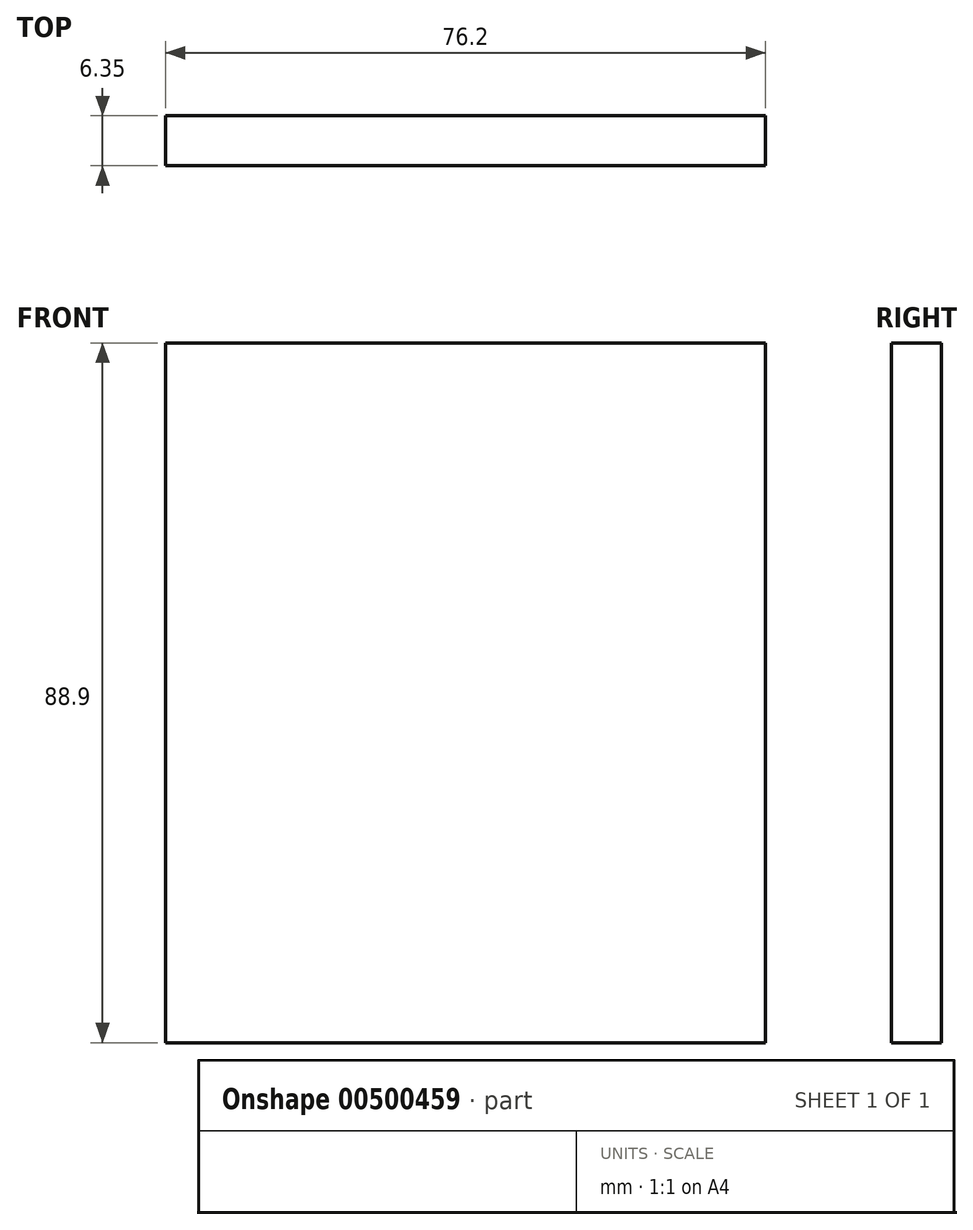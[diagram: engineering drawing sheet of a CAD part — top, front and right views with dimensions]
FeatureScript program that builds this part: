
annotation { "Feature Type Name" : "Feature", "Feature Type Description" : "" }
export const myFeature = defineFeature(function(context is Context, id is Id, definition is map)
    precondition{}
    {
        {
            var Q0;
            Q0=qCreatedBy(makeId("Front.planeOp"),FACE);
            var sketch = newSketch(context, id + "F0", { "sketchPlane" : qUnion([Q0])});
            skLineSegment(sketch, "E0.bottom", {"start": v(-36.9, 58.36) * mm, "end": v(39.3, 58.36) * mm});
            skLineSegment(sketch, "E0.top", {"start": v(-36.9, -30.54) * mm, "end": v(39.3, -30.54) * mm});
            skLineSegment(sketch, "E0.left", {"start": v(-36.9, 58.36) * mm, "end": v(-36.9, -30.54) * mm});
            skLineSegment(sketch, "E0.right", {"start": v(39.3, 58.36) * mm, "end": v(39.3, -30.54) * mm});
            skSolve(sketch);
        }
        {
            var Q0;
            Q0=makeQuery(id+"F0.imprint","IMPRINT",FACE,{"disambiguationData":[TD([[makeQuery(id+"F0.imprint","IMPRINT",EDGE,{"derivedFrom":sQuery(id+"F0.wireOp",EDGE,"E0.bottom")}),-1.0]])]});
            extrude(context, id + "F1", {"entities" : qUnion([Q0]), "depth" : 6.35 * mm});
        }
    });
